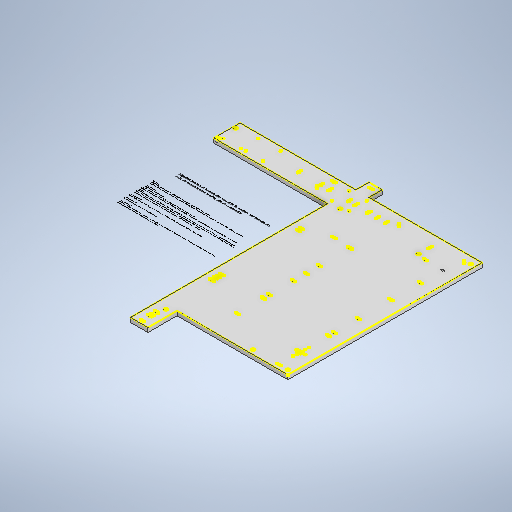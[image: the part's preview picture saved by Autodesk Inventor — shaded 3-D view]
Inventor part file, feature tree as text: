
AUTODESK INVENTOR PART (.ipt)
format: ipt  version: 2025.2 (Build 292293000, 293)  size: 1,577,472 bytes
history: native  units: in
note: dims shown in document units (in); Inventor stores cm internally (conversion verified against a paired STEP export)
features: extrude x26, other x16, sketch x11, hole x5, projected_geometry x4, move_body x3, plane x1, direct_edit x1
ambient origin geometry x8: Origin, YZ Plane, XZ Plane, XY Plane, X Axis, Y Axis, Z Axis, Center Point
bodies: Solid1 (feature_tree)
feature tree (67):
  other  "BoardMounting"
  plane  "Work Plane1"
  sketch  "Sketch2"  dims[d0=0.5in d1=0.5in]
  extrude  "Extrusion4"  Depth=0.5in
  extrude  "ForwardPathDowellPins"  Depth=0.25in
  extrude  "ReversePathDowellPins"  Depth=36.76in
  other  "CTASLMHoles"
  other  "VCSection"
  extrude  "VCPlate"  Depth=0.25in
  hole  "Hole1"  [1 undecoded]
  other  "BaseplateMountingHoles"
  extrude  "BaseplateMountingHolesInner"  Depth=3.175in
  extrude  "BaseplateMountingHolesOuter"  Depth=2.76in
  extrude  "CTASLMElementHolesTop"  Depth=2.577in
  extrude  "Extrusion10"  Depth=7.4961in
  extrude  "Extrusion11"  Depth=1.5in
  sketch  "Sketch8"  dims[d2=0.25in d3=0.4in]
  other  "CylindricalPath"
  other  "CylindricalPathOption1"
  other  "CylindricalPathOption2"
  other  "CylindricalPathOption3"
  other  "CylindricalPathOption3_CTaslmHoles"
  hole  "Hole2"  [1 undecoded]
  extrude  "Extrusion12"  Depth=0.25in
  other  "CylindricalPathOption4"
  hole  "Hole3"  [1 undecoded]
  other  "CylindricalPathOption4_CTaslmHoles"
  extrude  "Extrusion13"  Depth=0.25in
  direct_edit  "Direct Edit1"
  extrude  "CPO4_InnerHolesASLM"  Depth=0.25in
  extrude  "CPO4_InnerHolesCTASLM"  Depth=1.5in
  extrude  "CPO4_OuterHoles"  Depth=0.25in
  extrude  "CPO4_DowellPinsASLM"  Depth=1.5in
  extrude  "CPO4_DowelPinsCTASLM"  Depth=0.25in
  sketch  "Sketch22"  dims[d11=1.5in d12=0.5in]
  extrude  "Extrusion19"  Depth=0.25in
  extrude  "Extrusion20"  Depth=0.25in
  extrude  "Extrusion21"  Depth=0.5in
  extrude  "Extrusion22"  Depth=0.25in
  sketch  "Sketch24"  dims[d15=0.665in d16=2.76in]
  other  "Additional Alignment Holes Top"
  hole  "Hole4"  [1 undecoded]
  extrude  "Extrusion23"  Depth=0.25in
  extrude  "Extrusion24"  Depth=0.25in
  extrude  "Extrusion25"  Depth=0.25in
  sketch  "Sketch27"  dims[d19=10.479in d20=7.4961in]
  extrude  "Extrusion26"  Depth=0.25in
  extrude  "Extrusion27"  Depth=0.25in
  extrude  "Extrusion28"  Depth=0.25in
  hole  "Hole5"  [1 undecoded]
  sketch  "Sketch29"  dims[d23=2.0in d24=0.25in d25=0.197in d26=0.197in d27=0.0797in d28=0.0797in d29=0.25in d30=0.197in d31=0.197in d32=0.0797in d33=0.0797in d34=0.25in d35=0.197in d36=0.197in d37=0.0797in d38=0.0797in d39=0.25in d40=0.197in d41=0.197in d42=0.0797in d43=0.0797in d44=0.25in d45=0.197in d46=0.197in d47=0.0797in d48=0.0797in d49=0.25in d50=0.197in d51=0.197in d52=0.0797in d53=0.0797in d54=0.25in d55=0.197in d56=0.197in d57=0.0797in d58=0.0797in d59=0.25in d60=0.197in d61=0.197in d62=0.0797in d63=0.0797in d64=0.25in d65=0.197in d66=0.197in d67=0.08in d68=0.08in d69=0.25in d70=0.197in d71=0.197in d72=0.08in d73=0.08in d74=0.25in d75=0.197in d76=0.197in d77=0.08in d78=0.08in d81=0.175in d82=0.0in d83=1.5in d84=8.979in d85=1.5in d86=7.4961in d87=6.021in d88=1.0in d89=0.5in d90=0.4738in d91=0.4738in d92=0.25in d93=0.0797in d94=0.0797in d95=0.4738in d96=0.4738in d97=0.25in d98=0.0797in d99=0.0797in d100=0.25in d101=0.197in d102=0.197in d103=0.0797in d104=0.0797in d105=0.25in d106=0.197in d107=0.197in d108=0.0797in d109=0.0797in d110=0.25in d111=0.197in d112=0.0797in d113=0.0797in d114=0.25in d115=0.197in d116=0.0797in d117=0.0797in d118=0.5in d119=1.5in d120=0.5in d121=0.0in d122=0.75in d123=4.857in d124=9.8971in d125=6.8583in d126=1.5in d127=1.5in d128=0.5in d129=1.5in d130=0.25in d131=0.197in d132=0.197in d133=0.0797in d134=0.0797in d135=0.25in d136=0.197in d137=0.197in d138=0.0797in d139=0.0797in d140=0.25in d141=0.197in d142=0.197in d143=0.0797in d144=0.0797in d145=0.175in d146=0.0in d147=9.1809in d148=7.0827in d149=0.25in d150=0.197in d151=0.197in d152=0.0797in d153=0.0797in d154=0.25in d155=0.197in d156=0.197in d157=0.0797in d158=0.0797in d160=0.8752in d161=3.0276in d162=0.1061in d163=0.19in d164=1.5in d165=2.0in d166=1.0in d167=1.0in d168=1.0in d169=0.6in d170=0.5in d171=0.0in d172=0.196in d173=0.5in d174=0.375in d175=0.25in d176=0.5635in d177=1.0in d178=0.8108in d179=21.0in d180=27.0in d181=2.0in d182=14.0in d183=20.0in d184=2.0in d185=19.0in d186=0.4in d187=0.25in d188=0.4in d189=0.25in d190=0.4in d191=0.25in d192=0.4in d193=0.25in d194=0.4in d195=0.25in d196=0.4in d197=0.25in d198=0.4in d199=0.25in d200=0.4in d201=0.25in d202=0.4in d203=0.25in d204=0.4in d205=0.25in d206=0.5in d207=0.0in d208=0.3in d209=0.0in d210=2.0in d211=0.0in d212=0.175in d213=0.0in d214=0.4in d215=0.4in d216=0.4in d217=0.4in d218=0.4in d219=0.4in d220=0.4in d221=0.4in d222=0.4in d223=0.4in d224=0.4in d225=0.4in d226=0.4in d227=0.4in d228=0.4in d229=0.4in d230=0.4in d231=0.4in d232=0.4in d233=0.3in d234=0.0in d235=3.7433in d236=0.25in d237=0.0797in d238=0.0797in d239=0.4in d240=2.5in d241=0.75in d242=0.25in d243=0.0797in d244=0.0797in d245=1.0in d246=1.0in d247=9.1809in d248=7.0827in d249=0.25in d250=0.197in d251=0.197in d252=0.0797in d253=0.0797in d254=0.25in d255=0.197in d256=0.197in d257=0.0797in d258=0.0797in d264=0.25in d265=0.197in d266=0.197in d267=0.0797in d268=0.0797in d269=1.0in d270=1.0in d271=9.8971in d272=6.8583in d273=0.5in d274=1.5in d275=0.25in d276=0.197in d277=0.197in d278=0.0797in d279=0.0797in d280=0.25in d281=0.197in d282=0.197in d283=0.0797in d284=0.0797in d285=0.25in d286=0.197in d287=0.197in d288=0.0797in d289=0.0797in d290=1.0in d291=0.4in d292=0.4in d293=0.4in d294=0.4in d295=0.4in d296=0.4in d297=1.5in d298=0.5in d299=3.0in d300=0.6736in d301=2.7622in d302=1.5in d303=1.5in d304=3.6673in d305=6.9909in d306=1.5in d307=3.9528in d308=0.197in d309=0.197in d310=0.08in d311=0.08in d312=0.25in d313=0.197in d314=0.197in d315=0.08in d316=0.08in d317=0.25in d318=0.197in d319=0.197in d320=0.08in d321=0.08in d322=0.25in d323=0.197in d324=0.197in d325=0.08in d326=0.08in d327=0.25in d328=0.197in d329=0.197in d330=0.08in d331=0.08in d332=0.25in d333=0.197in d334=0.197in d335=0.08in d336=0.08in d337=0.25in d338=0.197in d339=0.197in d340=0.08in d341=0.08in d342=0.25in d343=0.197in d344=0.197in d345=0.08in d346=0.08in d347=0.25in d348=0.197in d349=0.197in d350=0.08in d351=0.08in d352=0.25in d353=0.197in d354=0.197in d355=0.08in d356=0.08in d357=0.25in d358=2.0in d359=0.08in d360=0.08in d361=0.25in d362=0.1509in d363=0.08in d364=0.08in d365=0.25in d366=1.5in d394=4.5in d395=2.4909in d396=0.4738in d397=0.4738in d398=0.25in d399=0.08in d400=0.08in d401=5.4909in d402=0.25in d403=1.5in d404=3.9528in d405=5.4638in d406=9.8801in d407=8.4055in d408=0.1984in d409=0.1984in d410=0.08in d411=0.08in d412=0.25in d413=0.1984in d414=0.1984in d415=0.08in d416=0.08in d417=0.25in d418=0.1984in d419=0.1984in d420=0.08in d421=0.08in d422=0.25in d423=0.4738in d424=0.4738in d425=0.25in d426=0.08in d427=0.08in d428=2.4909in d429=0.25in d430=1.5in d431=3.9528in d432=5.4638in d433=9.8801in d434=8.4055in d435=0.1984in d436=0.1984in d437=0.08in d438=0.08in d439=0.25in d440=0.1984in d441=0.1984in d442=0.08in d443=0.08in d444=0.25in d445=0.1984in d446=0.1984in d447=0.08in d448=0.08in d449=0.25in d450=1.5in d451=0.5in d452=3.0in d453=0.6736in d454=2.7622in d455=1.5in d456=1.5in d457=3.6673in d458=6.9909in d459=1.5in d460=3.9528in d461=0.197in d462=0.197in d463=0.08in d464=0.08in d465=0.25in d466=0.197in d467=0.197in d468=0.08in d469=0.08in d470=0.25in d471=0.197in d472=0.197in d473=0.08in d474=0.08in d475=0.25in d476=0.197in d477=0.197in d478=0.08in d479=0.08in d480=0.25in d481=0.197in d482=0.197in d483=0.08in d484=0.08in d485=0.25in d486=0.197in d487=0.197in d488=0.08in d489=0.08in d490=0.25in d491=0.197in d492=0.197in d493=0.08in d494=0.08in d495=0.25in d496=0.197in d497=0.197in d498=0.08in d499=0.08in d500=0.25in d501=0.197in d502=0.197in d503=0.08in d504=0.08in d505=0.25in d506=0.197in d507=0.197in d508=0.08in d509=0.08in d510=0.25in d511=2.0in d512=0.08in d513=0.08in d514=0.25in d515=0.1509in d516=0.08in d517=0.08in d518=0.25in d519=1.5in d520=4.5in d521=2.4909in d522=0.4738in d523=0.4738in d524=0.25in d525=0.08in d526=0.08in d527=2.4909in d528=0.25in d529=1.5in d530=3.9528in d531=5.4638in d532=9.8801in d533=8.4055in d534=0.1984in d535=0.1984in d536=0.08in d537=0.08in d538=0.25in d539=0.1984in d540=0.1984in d541=0.08in d542=0.08in d543=0.25in d544=0.1984in d545=0.1984in d546=0.08in d547=0.08in d548=0.25in d549=9.1634in d550=8.2568in d551=0.197in d552=0.197in d553=0.08in d554=0.08in d555=0.197in d556=0.197in d557=0.08in d558=0.08in d559=0.197in d560=0.197in d561=0.08in d562=0.08in d563=0.8752in d564=3.0276in d565=0.1061in d566=0.19in d567=1.5in d568=2.0in d569=1.0in d570=1.0in d571=1.0in d572=0.6in d573=0.196in d574=0.5in d575=0.375in d576=0.25in d577=0.5635in d578=1.0in d579=0.8108in d580=1.5in d581=0.5in d582=3.0in d583=0.5in d584=0.0in d585=1.5in d586=0.5in d587=3.0in d588=0.6736in d589=2.7622in d590=1.5in d591=1.5in d592=3.6673in d593=6.9909in d594=1.5in d595=3.9528in d596=0.197in d597=0.197in d598=0.0797in d599=0.0797in d600=0.25in d601=0.197in d602=0.197in d603=0.0797in d604=0.0797in d605=0.25in d606=0.197in d607=0.197in d608=0.0797in d609=0.0797in d610=0.25in d611=0.197in d612=0.197in d613=0.0797in d614=0.0797in d615=0.25in d616=0.197in d617=0.197in d618=0.0797in d619=0.0797in d620=0.25in d621=0.197in d622=0.197in d623=0.0797in d624=0.0797in d625=0.25in d626=0.197in d627=0.197in d628=0.0797in d629=0.0797in d630=0.25in d631=0.197in d632=0.197in d633=0.0797in d634=0.0797in d635=0.25in d636=0.197in d637=0.197in d638=0.0797in d639=0.0797in d640=0.25in d641=0.197in d642=0.197in d643=0.0797in d644=0.0797in d645=0.25in d646=2.0in d647=0.0797in d648=0.0797in d649=0.25in d650=0.1509in d651=0.0797in d652=0.0797in d653=0.25in d654=1.5in d655=4.5in d656=2.4909in d657=0.4738in d658=0.4738in d659=0.25in d660=0.0797in d661=0.0797in d662=2.4909in d663=0.25in d664=1.5in d665=3.9528in d684=0.8752in d685=3.0276in d686=0.1061in d687=0.19in d688=1.5in d689=2.0in d690=1.0in d691=1.0in d692=1.0in d693=0.6in d694=0.196in d695=0.5in d696=0.375in d697=0.25in d698=0.5635in d699=1.0in d700=0.8108in d701=0.75in d704=8.4055in d709=0.25in d714=0.25in d719=0.25in d720=9.1634in d721=8.2568in d722=0.197in d723=0.197in d724=0.0797in d725=0.0797in d726=0.197in d727=0.197in d728=0.0797in d729=0.0797in d730=0.197in d731=0.197in d732=0.0797in d733=0.0797in d734=0.5in d735=0.0in d736=0.0in d737=0.0in d738=-0.5in d739=0.0in d740=0.0in d741=-0.5in d742=0.0in d743=0.0in d744=1.0in d745=0.5in d746=0.0in d747=0.5in d748=0.0in d749=0.4in d750=0.4in d751=0.4in d752=0.4in d753=0.4in d754=0.4in d755=0.4in d756=0.4in d757=0.4in d758=0.4in d759=0.4in d760=0.4in d761=0.4in d762=0.4in d763=0.4in d764=0.4in d765=0.3in d766=0.0in d767=0.0797in d768=0.0797in d769=0.0797in d770=0.0797in d771=0.197in d772=0.0797in d773=0.175in d774=0.0in d775=0.175in d776=0.0in d777=2.5in d778=0.197in d779=0.197in d780=0.197in d781=0.197in d782=0.197in d783=0.197in d784=0.197in d785=0.197in d786=0.0797in d787=0.0797in d788=0.0797in d789=0.0797in d790=0.0797in d791=0.197in d792=0.0797in d793=0.0797in d794=0.0797in d795=0.5in d796=0.75in d797=0.75in d798=0.5in d799=0.0in d800=0.175in d801=0.0in d802=1.0in d803=0.0in d804=0.4in d805=0.3in d806=0.0in d807=0.2382in d808=0.25in d809=0.0797in d810=0.0797in d811=0.75in d812=0.25in d813=0.0797in d814=0.0797in d815=1.0in d816=0.25in d817=0.0797in d818=0.0797in d819=1.0in d820=0.25in d821=0.0797in d822=0.0797in d823=5.0in d824=0.25in d825=0.0797in d826=0.0797in d827=1.0in d828=1.0in d829=1.0in d830=2.0in d831=2.0in d832=0.196in d833=0.5in d834=0.375in d835=0.25in d836=0.5635in d837=1.0in d838=0.8108in d839=1.0in d840=0.0in d841=0.175in d842=0.0in d844=0.4in d845=0.4in d846=0.4in d847=0.4in d848=0.4in d849=0.3in d850=0.0in d853=0.5in d854=0.25in d855=0.5in d856=0.5in d857=0.5in d858=0.25in d859=0.25in d860=0.8661in d861=0.8661in d862=0.8661in d863=0.1191in d864=0.1191in d865=1.0in d866=0.0in d867=0.175in d868=0.0in d869=0.4in d870=0.4in d871=0.3in d872=0.0in d873=0.196in d874=0.5in d875=0.375in d876=0.25in d877=0.5635in d878=1.0in d879=0.8108in d880=0.1576in d881=0.25in d882=0.197in d883=0.197in d884=0.0797in d885=0.0797in d886=0.4in]
  other  "ElementHolesBottom"
  other  "CYlindricalPathOption3_VCHoles"
  sketch  "Sketch16"  dims[d4=4.0in d5=36.76in]
  other  "CylindricalPathOption4_VCHoles"
  sketch  "Sketch20"  dims[d6=0.25in d7=0.4in d8=5.0in]
  other  "MountHolesOuter_CylindricalOption4"
  projected_geometry  "Projected Loop90"
  projected_geometry  "Projected Loop92"
  projected_geometry  "Projected Loop93"
  sketch  "Sketch23"  dims[d13=2.5in d14=3.175in]
  sketch  "Sketch26"  dims[d17=7.104in d18=2.577in]
  sketch  "Sketch28"  dims[d21=1.5in d22=0.1509in]
  projected_geometry  "Projected Loop94"
  move_body  "Move1"
  move_body  "Move2"
  move_body  "Move3"
note: 5 required parameter values undecoded (feature->parameter linkage not recoverable at this tier; creation-order binding heuristic only, values carry confidence <= 0.55)
